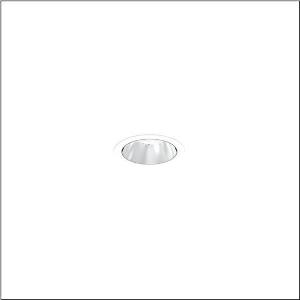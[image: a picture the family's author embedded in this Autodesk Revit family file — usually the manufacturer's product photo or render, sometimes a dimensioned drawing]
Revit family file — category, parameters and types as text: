
# Revit family: lunis_21_s_51db15ma91c
name_source: partatom
category: Lighting Fixtures
units: mm (PartAtom-declared; Revit-internal decimal feet)

## family parameters
Cut with Voids When Loaded = No
Host = Face
Light Source = No
Part Type = Normal
Room Calculation Point = No
Round Connector Dimension = Use Diameter
Shared = No

## types (1)
- --- (1 x LED, 980 lm, 5.9 W, 6500K)
    Apparent Load = 6 VA
    CIE Flux Codes = 93 99 100 100 100
    Color Rendering = 80
    Color Temperature = 6500K
    Default Elevation = 1800 mm
    Description = Lunis 21,  S, downlight, light control with lens, of PMMA, anti glare with reflector, of PC, highly specular, light emission: direct distribution, LED rated luminous flux: 990lm, light colour: 830/840/865, with terminal, 3-pole, mains connection: 220..240V, AC, 50..60Hz, housing, round, of diecast aluminium, traffic white (RAL 9016), diameter: 84mm, clamping range: 1..40mm, protection rating (complete): IP20, protection rating (on room side): IP54, insulation class (complete): insulation class II (safety insulation), certification: CE, impact resistance: IK03, packaging unit: 1 piece
    Height = 0 mm  [stored 0 ft]
    Lamp = 1 x LED
    Lamp Light Flux = 980 lm
    Lamp Power = 5.9 W
    Lamp count = 1
    Length = 84 mm
    Luminous efficacy = 166 lm/W
    Manufacturer = Siteco
    ModVariant = No
    Model = 51DB15MA91C
    Mounting Place = Ceiling
    Mounting Type = Recessed
    Number of Poles = 1
    OnlyDefault = Yes
    Power Factor = 1
    Product Name = Lunis 21 S
    Product group = downlight
    ProductGroupID = 400
    Protection Class = Protection class II
    Protection Degree = IP 20
    RLX_Detail_Level = 1
    RLX_Emergency_Light_Flux = 0 lm
    RLX_Emergency_Type = 0
    RLX_Emergency_Type_DB = No
    RlxData = <blob elided: 8369 chars, md5=6a01854a>
    Socket = socket
    Standby Power = 0 W
    System Light Flux = 980 lm
    System Power = 6 W
    Type Comments = individual setting: colour temperature 6500K
    Type Image = l_1290840.jpg
    URL = http://relux.com
    VarID = @adj_015418
    Voltage = 0 V
    Weight = 0.00 kg
    Width = 0 mm  [stored 0 ft]

note: [stored X ft] marks values corroborated as IEEE doubles in the binary element streams (Revit-internal decimal feet)

## geometry (parser evidence)
native form markers: Sweep x10
no freeform markers — native parametric forms only
